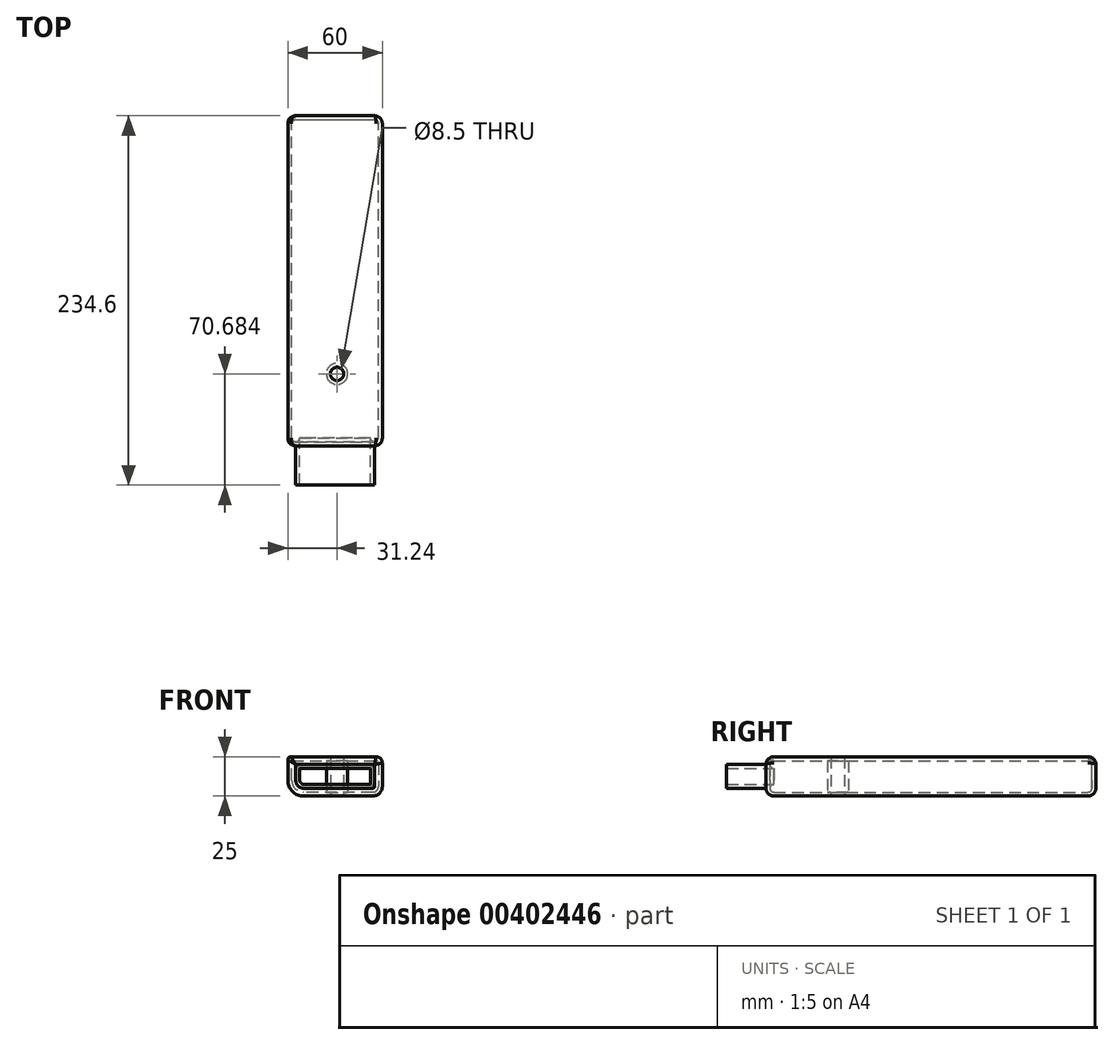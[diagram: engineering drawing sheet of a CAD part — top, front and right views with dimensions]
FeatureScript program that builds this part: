
annotation { "Feature Type Name" : "Feature", "Feature Type Description" : "" }
export const myFeature = defineFeature(function(context is Context, id is Id, definition is map)
    precondition{}
    {
        {
            var Q0;
            Q0=qCreatedBy(makeId("Front.planeOp"),FACE);
            var sketch = newSketch(context, id + "F0", { "sketchPlane" : qUnion([Q0])});
            skLineSegment(sketch, "E0", {"start": v(0, 10) * mm, "end": v(0, 23) * mm});
            skLineSegment(sketch, "E1", {"start": v(2, 25) * mm, "end": v(56, 25) * mm});
            skLineSegment(sketch, "E2", {"start": v(60, 21) * mm, "end": v(60, 6) * mm});
            skLineSegment(sketch, "E3", {"start": v(54, 0) * mm, "end": v(10, 0) * mm});
            skPoint(sketch, "E4.visualSharp", {"position": v(0, 25) * mm});
            skArc(sketch, "E4.filletArc", {"start": v(2, 25) * mm, "mid": v(0.59, 24.41) * mm, "end": v(0, 23) * mm});
            skPoint(sketch, "E5.visualSharp", {"position": v(60, 25) * mm});
            skArc(sketch, "E5.filletArc", {"start": v(60, 21) * mm, "mid": v(58.83, 23.83) * mm, "end": v(56, 25) * mm});
            skPoint(sketch, "E6.visualSharp", {"position": v(60, 0) * mm});
            skArc(sketch, "E6.filletArc", {"start": v(54, 0) * mm, "mid": v(58.24, 1.76) * mm, "end": v(60, 6) * mm});
            skPoint(sketch, "E7.visualSharp", {"position": v(0, 0) * mm});
            skArc(sketch, "E7.filletArc", {"start": v(0, 10) * mm, "mid": v(2.93, 2.93) * mm, "end": v(10, 0) * mm});
            skSolve(sketch);
        }
        {
            var Q0;
            Q0=makeQuery(id+"F0.imprint","IMPRINT",FACE,{"disambiguationData":[TD([[makeQuery(id+"F0.imprint","IMPRINT",EDGE,{"derivedFrom":sQuery(id+"F0.wireOp",EDGE,"E0")}),-1.0]])]});
            extrude(context, id + "F1", {"entities" : qUnion([Q0]), "depth" : 209.6 * mm});
        }
        {
            var Q0;
            Q0=makeQuery(id+"F1.opExtrude","SWEPT_EDGE",EDGE,{"disambiguationData":[OSD([sQuery(id+"F0.wireOp",EDGE,"E1"),sQuery(id+"F0.wireOp",EDGE,"E2")])]});
            var Q1;
            Q1=makeQuery(id+"F1.opExtrude","SWEPT_EDGE",EDGE,{"disambiguationData":[OSD([sQuery(id+"F0.wireOp",EDGE,"E0"),sQuery(id+"F0.wireOp",EDGE,"E1")])]});
            var Q2;
            Q2=makeQuery(id+"F1.opExtrude","CAP_EDGE",EDGE,{"disambiguationData":[OSD([sQuery(id+"F0.wireOp",EDGE,"E1")])],"isStart":false});
            var Q3;
            Q3=makeQuery(id+"F1.opExtrude","CAP_EDGE",EDGE,{"disambiguationData":[OSD([sQuery(id+"F0.wireOp",EDGE,"E1")])],"isStart":true});
            var Q4;
            Q4=makeQuery(id+"F1.opExtrude","CAP_EDGE",EDGE,{"disambiguationData":[OSD([sQuery(id+"F0.wireOp",EDGE,"E0")])],"isStart":false});
            var Q5;
            Q5=makeQuery(id+"F1.opExtrude","CAP_EDGE",EDGE,{"disambiguationData":[OSD([sQuery(id+"F0.wireOp",EDGE,"E2")])],"isStart":false});
            fillet(context, id + "F2", {"entities" : qUnion([Q0, Q1, Q2, Q3, Q4, Q5]), "radius" : 5 * mm, "tangentPropagation" : true, "allowEdgeOverflow" : false});
        }
        {
            var Q0;
            Q0=makeQuery(id+"F1.opExtrude","SWEPT_FACE",FACE,{"disambiguationData":[OSD([sQuery(id+"F0.wireOp",EDGE,"E1")])]});
            var sketch = newSketch(context, id + "F3", { "sketchPlane" : qUnion([Q0])});
            skPoint(sketch, "E8", {"position": v(31.24, -163.92) * mm});
            skSolve(sketch);
        }
        {
            var Q0;
            Q0=sQuery(id+"F3.wireOp",VERTEX,"E8");
            var Q1;
            Q1=makeQuery(id+"F1.opExtrude","SWEPT_BODY",BODY,{"disambiguationData":[OSD([sQuery(id+"F0.wireOp",EDGE,"E0"),sQuery(id+"F0.wireOp",EDGE,"E1"),sQuery(id+"F0.wireOp",EDGE,"E2"),sQuery(id+"F0.wireOp",EDGE,"E3"),sQuery(id+"F0.wireOp",EDGE,"E4.filletArc"),sQuery(id+"F0.wireOp",EDGE,"E5.filletArc"),sQuery(id+"F0.wireOp",EDGE,"E6.filletArc"),sQuery(id+"F0.wireOp",EDGE,"E7.filletArc")])]});
            hole(context, id + "F4", {"style" : HoleStyle.SIMPLE, "endStyle" : HoleEndStyle.BLIND, "standardTappedOrClearance" : lookupTablePath({ "standard" : "ISO", "engagement" : "75%", "pitch" : "1.5 mm", "size" : "M10", "type" : "Tapped" }), "standardBlindInLast" : lookupTablePath({ "standard" : "ISO", "engagement" : "75%", "pitch" : "1.5 mm", "size" : "M10", "type" : "Tapped" }), "holeDiameter" : 8.5 * mm, "showTappedDepth" : true, "holeDepth" : 27.25 * mm, "isTappedThrough" : true, "tappedDepth" : 22.75 * mm, "tapClearance" : 3, "locations" : qUnion([Q0]), "scope" : qUnion([Q1]), "majorDiameter" : 10 * mm, "startStyle" : HoleStartStyle.SKETCH});
        }
        {
            var Q0;
            Q0=makeQuery(id+"F1.opExtrude","CAP_FACE",FACE,{"disambiguationData":[OSD([sQuery(id+"F0.wireOp",EDGE,"E0"),sQuery(id+"F0.wireOp",EDGE,"E1"),sQuery(id+"F0.wireOp",EDGE,"E2"),sQuery(id+"F0.wireOp",EDGE,"E3"),sQuery(id+"F0.wireOp",EDGE,"E4.filletArc"),sQuery(id+"F0.wireOp",EDGE,"E5.filletArc"),sQuery(id+"F0.wireOp",EDGE,"E6.filletArc"),sQuery(id+"F0.wireOp",EDGE,"E7.filletArc")])],"isStart":false});
            extrude(context, id + "F5", {"entities" : qUnion([Q0]), "operationType" : NewBodyOperationType.ADD, "depth" : 25 * mm});
        }
        {
            var Q0;
            Q0=makeQuery(id+"F5.opExtrude","CAP_FACE",FACE,{"disambiguationData":[OSD([sQuery(id+"F0.wireOp",EDGE,"E0"),sQuery(id+"F0.wireOp",EDGE,"E1"),sQuery(id+"F0.wireOp",EDGE,"E2"),sQuery(id+"F0.wireOp",EDGE,"E3"),sQuery(id+"F0.wireOp",EDGE,"E4.filletArc"),sQuery(id+"F0.wireOp",EDGE,"E5.filletArc"),sQuery(id+"F0.wireOp",EDGE,"E6.filletArc"),sQuery(id+"F0.wireOp",EDGE,"E7.filletArc")])],"isStart":false});
            shell(context, id + "F6", {"entities" : qUnion([Q0]), "thickness" : 2.5 * mm});
        }
    });
